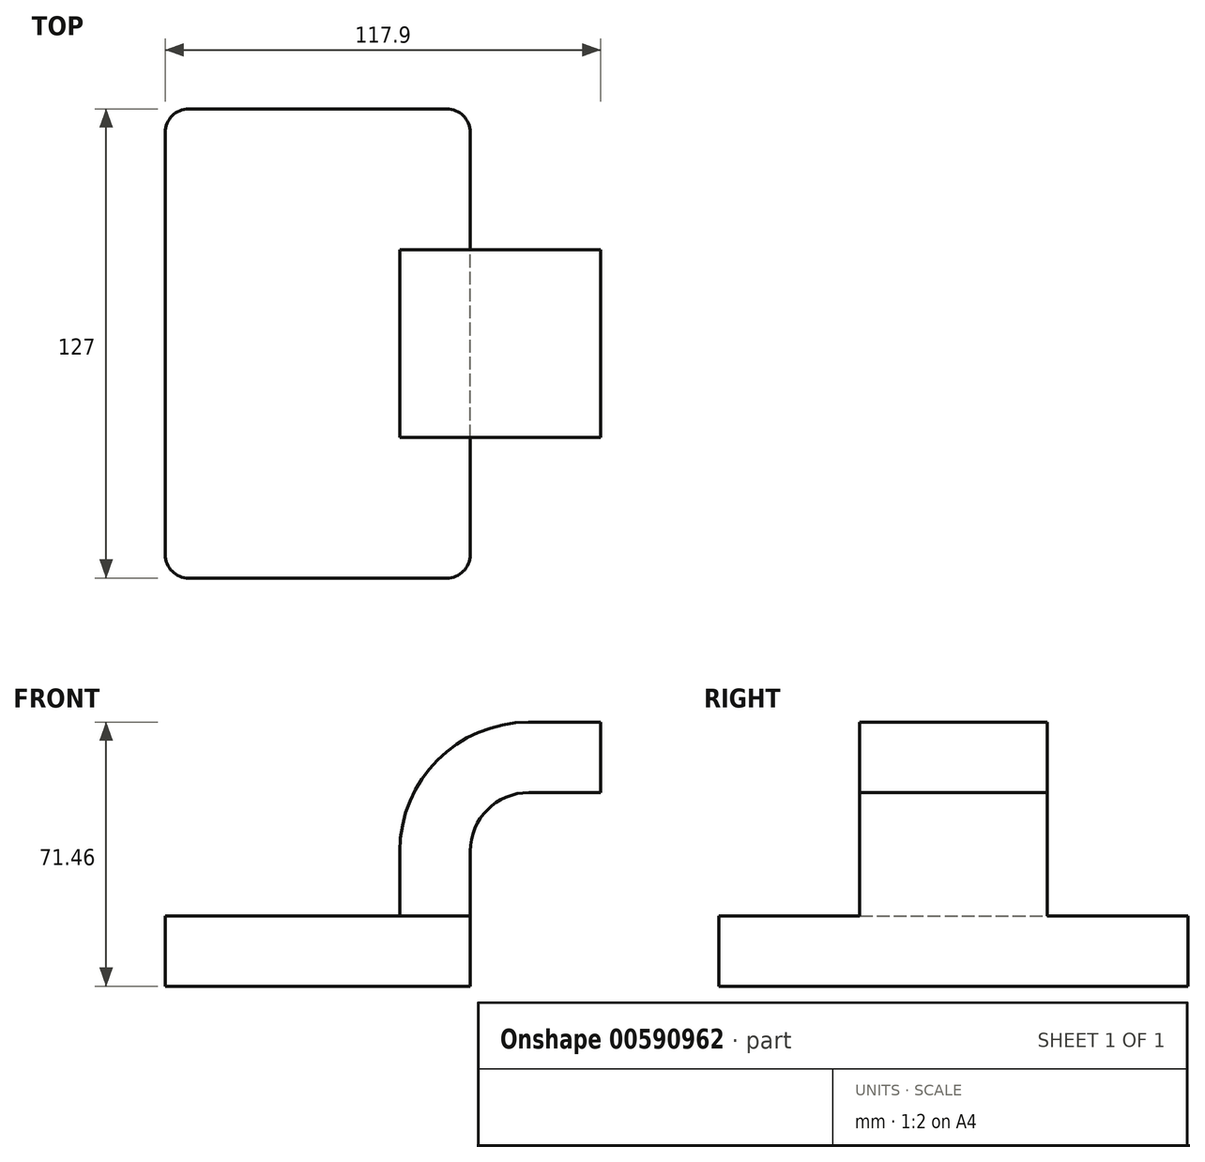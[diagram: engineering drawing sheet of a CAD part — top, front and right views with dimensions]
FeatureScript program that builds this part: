
annotation { "Feature Type Name" : "Feature", "Feature Type Description" : "" }
export const myFeature = defineFeature(function(context is Context, id is Id, definition is map)
    precondition{}
    {
        {
            var Q0;
            Q0=qCreatedBy(makeId("Front.planeOp"),FACE);
            var sketch = newSketch(context, id + "F0", { "sketchPlane" : qUnion([Q0])});
            skLineSegment(sketch, "E0.bottom", {"start": v(-41.28, 9.52) * mm, "end": v(41.28, 9.53) * mm});
            skLineSegment(sketch, "E0.top", {"start": v(-41.28, -9.53) * mm, "end": v(41.28, -9.53) * mm});
            skLineSegment(sketch, "E0.left", {"start": v(-41.28, 9.52) * mm, "end": v(-41.27, -9.53) * mm});
            skLineSegment(sketch, "E0.right", {"start": v(41.28, 9.53) * mm, "end": v(41.28, -9.52) * mm});
            skPoint(sketch, "E0.middle", {"position": v(0, 0) * mm});
            skLineSegment(sketch, "E1.bottom", {"start": v(111.13, 38.1) * mm, "end": v(60.33, 38.1) * mm});
            skLineSegment(sketch, "E1.top", {"start": v(111.13, 66.68) * mm, "end": v(60.33, 66.67) * mm});
            skLineSegment(sketch, "E1.left", {"start": v(111.13, 38.1) * mm, "end": v(111.13, 66.68) * mm});
            skLineSegment(sketch, "E1.right", {"start": v(60.33, 38.1) * mm, "end": v(60.33, 66.67) * mm});
            skPoint(sketch, "E1.middle", {"position": v(85.73, 52.39) * mm});
            skLineSegment(sketch, "E2", {"start": v(41.27, 9.53) * mm, "end": v(41.27, 27) * mm});
            skArc(sketch, "E3", {"start": v(41.27, 27) * mm, "mid": v(45.92, 38.23) * mm, "end": v(57.15, 42.88) * mm});
            skLineSegment(sketch, "E4", {"start": v(57.15, 42.88) * mm, "end": v(76.63, 42.88) * mm});
            skLineSegment(sketch, "E5.0", {"start": v(57.15, 61.93) * mm, "end": v(76.63, 61.93) * mm});
            skArc(sketch, "E5.1", {"start": v(22.22, 27) * mm, "mid": v(32.45, 51.7) * mm, "end": v(57.15, 61.93) * mm});
            skLineSegment(sketch, "E5.2", {"start": v(22.23, 9.53) * mm, "end": v(22.23, 27) * mm});
            skLineSegment(sketch, "E6", {"start": v(76.63, 42.88) * mm, "end": v(76.63, 61.93) * mm});
            skLineSegment(sketch, "E7", {"start": v(76.63, 38.1) * mm, "end": v(76.63, 42.88) * mm});
            skLineSegment(sketch, "E8", {"start": v(76.63, 61.93) * mm, "end": v(76.63, 66.68) * mm});
            skFitSpline(sketch, "E9", {"points": [v(-41.28, 9.53) * mm, v(57.15, 61.93) * mm], "startDerivative": vector(0.14, 73.53) * mm, "endDerivative": vector(134.6, 0.14) * mm});
            skSolve(sketch);
        }
        {
            var Q0;
            Q0=makeQuery(id+"F0.imprint","IMPRINT",FACE,{"disambiguationData":[TD([[makeQuery(id+"F0.imprint","IMPRINT",EDGE,{"derivedFrom":sQuery(id+"F0.wireOp",EDGE,"E0.top")}),1.0]])]});
            extrude(context, id + "F1", {"entities" : qUnion([Q0]), "endBound" : BoundingType.SYMMETRIC, "depth" : 127 * mm, "offsetDistance" : 25.4 * mm});
        }
        {
            var Q0;
            {var subQ5=sQuery(id+"F0.wireOp",EDGE,"E2");Q0=makeQuery(id+"F0.imprint","IMPRINT",FACE,{"disambiguationData":[TD([[makeQuery(id+"F0.imprint","IMPRINT",EDGE,{"derivedFrom":subQ5}),1.0]])]});}
            var Q1;
            {var subQ5=sQuery(id+"F0.wireOp",EDGE,"E6");Q1=makeQuery(id+"F0.imprint","IMPRINT",FACE,{"disambiguationData":[TD([[makeQuery(id+"F0.imprint","IMPRINT",EDGE,{"derivedFrom":subQ5}),1.0]])]});}
            extrude(context, id + "F2", {"entities" : qUnion([Q0, Q1]), "operationType" : NewBodyOperationType.ADD, "endBound" : BoundingType.SYMMETRIC, "depth" : 50.8 * mm, "offsetDistance" : 25.4 * mm});
        }
        {
            var Q0;
            {var subQ4=sQuery(id+"F0.wireOp",EDGE,"E5.1");Q0=makeQuery(id+"F0.imprint","IMPRINT",FACE,{"disambiguationData":[TD([[makeQuery(id+"F0.imprint","IMPRINT",EDGE,{"derivedFrom":subQ4}),1.0]])]});}
            extrude(context, id + "F3", {"entities" : qUnion([Q0]), "operationType" : NewBodyOperationType.ADD, "endBound" : BoundingType.SYMMETRIC, "depth" : 15.88 * mm, "offsetDistance" : 25.4 * mm});
        }
        {
            var Q0;
            Q0=makeQuery(id+"F1.opExtrude","CAP_EDGE",EDGE,{"disambiguationData":[OSD([sQuery(id+"F0.wireOp",EDGE,"E0.left")])],"isStart":true});
            var Q1;
            Q1=makeQuery(id+"F1.opExtrude","CAP_EDGE",EDGE,{"disambiguationData":[OSD([sQuery(id+"F0.wireOp",EDGE,"E0.left")])],"isStart":false});
            var Q2;
            Q2=makeQuery(id+"F1.opExtrude","CAP_EDGE",EDGE,{"disambiguationData":[OSD([sQuery(id+"F0.wireOp",EDGE,"E0.right")])],"isStart":false});
            var Q3;
            Q3=makeQuery(id+"F1.opExtrude","CAP_EDGE",EDGE,{"disambiguationData":[OSD([sQuery(id+"F0.wireOp",EDGE,"E0.right")])],"isStart":true});
            fillet(context, id + "F4", {"entities" : qUnion([Q0, Q1, Q2, Q3]), "radius" : 6.35 * mm, "tangentPropagation" : true, "allowEdgeOverflow" : false});
        }
    });
